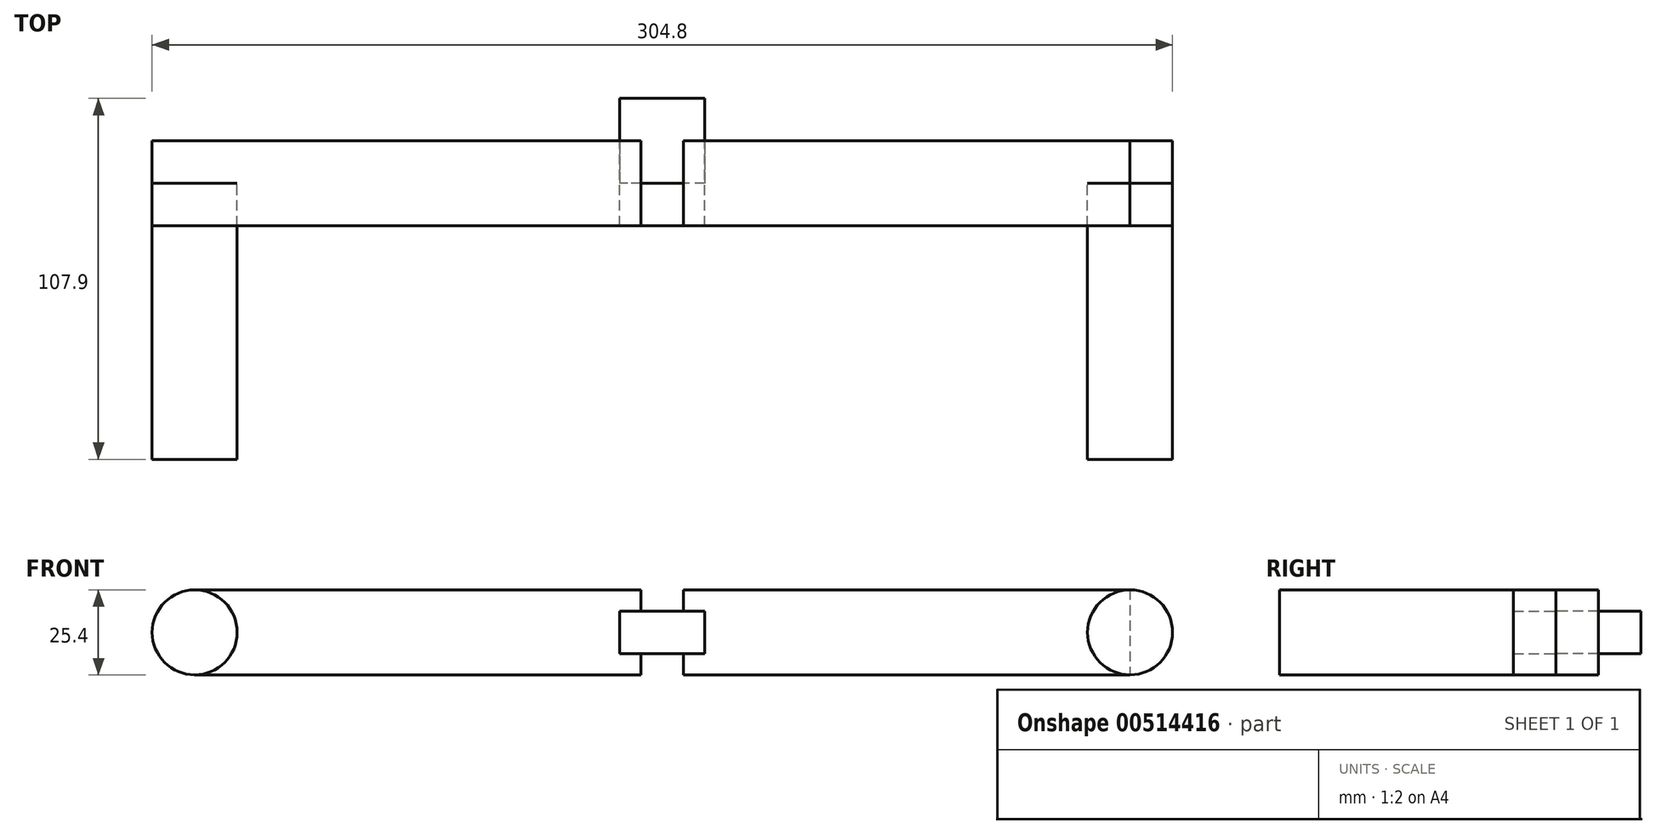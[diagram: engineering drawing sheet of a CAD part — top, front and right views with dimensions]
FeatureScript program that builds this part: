
annotation { "Feature Type Name" : "Feature", "Feature Type Description" : "" }
export const myFeature = defineFeature(function(context is Context, id is Id, definition is map)
    precondition{}
    {
        {
            var Q0;
            Q0=qCreatedBy(makeId("Front.planeOp"),FACE);
            var sketch = newSketch(context, id + "F0", { "sketchPlane" : qUnion([Q0])});
            skLineSegment(sketch, "E0.bottom", {"start": v(-139.7, 12.7) * mm, "end": v(139.7, 12.7) * mm});
            skLineSegment(sketch, "E0.top", {"start": v(-139.7, -12.7) * mm, "end": v(139.7, -12.7) * mm});
            skLineSegment(sketch, "E0.left", {"start": v(-139.7, 12.7) * mm, "end": v(-139.7, -12.7) * mm});
            skLineSegment(sketch, "E0.right", {"start": v(139.7, 12.7) * mm, "end": v(139.7, -12.7) * mm});
            skCircle(sketch, "E1", {"center": v(139.7, 0) * mm, "radius": 12.7 * mm});
            skArc(sketch, "E2", {"start": v(-139.7, 12.7) * mm, "mid": v(-152.4, 0) * mm, "end": v(-139.7, -12.7) * mm});
            skLineSegment(sketch, "E3", {"start": v(-139.7, 0) * mm, "end": v(-152.4, 0) * mm});
            skCircle(sketch, "E4", {"center": v(-139.7, 0) * mm, "radius": 12.7 * mm});
            skLineSegment(sketch, "E5.bottom", {"start": v(139.7, 12.7) * mm, "end": v(139.7, 12.7) * mm});
            skLineSegment(sketch, "E5.top", {"start": v(139.7, -12.7) * mm, "end": v(139.7, -12.7) * mm});
            skLineSegment(sketch, "E6.bottom", {"start": v(6.35, 12.7) * mm, "end": v(-6.35, 12.7) * mm});
            skLineSegment(sketch, "E6.top", {"start": v(6.35, -12.7) * mm, "end": v(-6.35, -12.7) * mm});
            skLineSegment(sketch, "E6.left", {"start": v(6.35, 12.7) * mm, "end": v(6.35, -12.7) * mm});
            skLineSegment(sketch, "E6.right", {"start": v(-6.35, 12.7) * mm, "end": v(-6.35, -12.7) * mm});
            skLineSegment(sketch, "E7.bottom", {"start": v(12.7, 6.35) * mm, "end": v(-12.7, 6.35) * mm});
            skLineSegment(sketch, "E7.top", {"start": v(12.7, -6.35) * mm, "end": v(-12.7, -6.35) * mm});
            skLineSegment(sketch, "E7.left", {"start": v(12.7, 6.35) * mm, "end": v(12.7, -6.35) * mm});
            skLineSegment(sketch, "E7.right", {"start": v(-12.7, 6.35) * mm, "end": v(-12.7, -6.35) * mm});
            skSolve(sketch);
        }
        {
            var Q0;
            {var subQ3=sQuery(id+"F0.wireOp",EDGE,"E3");Q0=makeQuery(id+"F0.imprint","IMPRINT",FACE,{"disambiguationData":[TD([[makeQuery(id+"F0.imprint","IMPRINT",EDGE,{"derivedFrom":subQ3}),-1.0]])]});}
            var Q1;
            {var subQ1=sQuery(id+"F0.wireOp",EDGE,"E0.left");var subQ3=makeQuery(id+"F0.imprint","INTERSECT",VERTEX,{"derivedFrom":[subQ1,sQuery(id+"F0.wireOp",EDGE,"E3")]});Q1=makeQuery(id+"F0.imprint","IMPRINT",FACE,{"disambiguationData":[TD([[makeQuery(id+"F0.imprint","IMPRINT",EDGE,{"disambiguationData":[TD([[subQ3,1.0]])],"derivedFrom":subQ1}),1.0]])]});}
            var Q2;
            {var subQ3=sQuery(id+"F0.wireOp",EDGE,"E3");Q2=makeQuery(id+"F0.imprint","IMPRINT",FACE,{"disambiguationData":[TD([[makeQuery(id+"F0.imprint","IMPRINT",EDGE,{"derivedFrom":subQ3}),1.0]])]});}
            var Q3;
            {var subQ0=sQuery(id+"F0.wireOp",EDGE,"E1");var subQ1=makeQuery(id+"F0.imprint","INTERSECT",VERTEX,{"derivedFrom":[sQuery(id+"F0.wireOp",EDGE,"E0.bottom"),subQ0]});Q3=makeQuery(id+"F0.imprint","IMPRINT",FACE,{"disambiguationData":[TD([[makeQuery(id+"F0.imprint","IMPRINT",EDGE,{"disambiguationData":[TD([[subQ1,-1.0]])],"derivedFrom":subQ0}),1.0]])]});}
            var Q4;
            {var subQ0=sQuery(id+"F0.wireOp",EDGE,"E0.right");Q4=makeQuery(id+"F0.imprint","IMPRINT",FACE,{"disambiguationData":[TD([[makeQuery(id+"F0.imprint","IMPRINT",EDGE,{"derivedFrom":subQ0}),1.0]])]});}
            var Q5;
            {var subQ0=sQuery(id+"F0.wireOp",EDGE,"E0.right");Q5=makeQuery(id+"F0.imprint","IMPRINT",FACE,{"disambiguationData":[TD([[makeQuery(id+"F0.imprint","IMPRINT",EDGE,{"derivedFrom":subQ0}),1.0]])]});}
            var Q6;
            {var subQ0=sQuery(id+"F0.wireOp",EDGE,"E0.left");var subQ4=makeQuery(id+"F0.imprint","INTERSECT",VERTEX,{"derivedFrom":[sQuery(id+"F0.wireOp",EDGE,"E3"),subQ0]});Q6=makeQuery(id+"F0.imprint","IMPRINT",FACE,{"disambiguationData":[TD([[makeQuery(id+"F0.imprint","IMPRINT",EDGE,{"disambiguationData":[TD([[subQ4,1.0]])],"derivedFrom":subQ0}),1.0]])]});}
            var Q7;
            Q7=sQuery(id+"F0.wireOp",EDGE,"E1");
            extrude(context, id + "F1", {"entities" : qUnion([Q0, Q1, Q2, Q3, Q4, Q5, Q6]), "surfaceEntities" : qUnion([Q7]), "depth" : 82.5 * mm, "offsetDistance" : 25.4 * mm});
        }
        {
            var Q0;
            {var subQ2=sQuery(id+"F0.wireOp",EDGE,"E0.bottom");var subQ4=sQuery(id+"F0.wireOp",EDGE,"E1");var subQ5=makeQuery(id+"F0.imprint","INTERSECT",VERTEX,{"derivedFrom":[subQ2,subQ4]});Q0=makeQuery(id+"F0.imprint","IMPRINT",FACE,{"disambiguationData":[TD([[makeQuery(id+"F0.imprint","IMPRINT",EDGE,{"disambiguationData":[TD([[subQ5,-1.0]])],"derivedFrom":subQ4}),-1.0]])]});}
            var Q1;
            {var subQ0=sQuery(id+"F0.wireOp",EDGE,"E0.right");Q1=makeQuery(id+"F0.imprint","IMPRINT",FACE,{"disambiguationData":[TD([[makeQuery(id+"F0.imprint","IMPRINT",EDGE,{"derivedFrom":subQ0}),-1.0]])]});}
            var Q2;
            {var subQ1=sQuery(id+"F0.wireOp",EDGE,"5lEPmECd-of7d-YvdJ-hnNs-EzF3xCs3axzf.bottom");Q2=makeQuery(id+"F0.imprint","IMPRINT",FACE,{"disambiguationData":[TD([[makeQuery(id+"F0.imprint","IMPRINT",EDGE,{"derivedFrom":subQ1}),-1.0]])]});}
            var Q3;
            Q3=makeQuery(id+"F0.imprint","IMPRINT",FACE,{"disambiguationData":[TD([[makeQuery(id+"F0.imprint","IMPRINT",EDGE,{"derivedFrom":sQuery(id+"F0.wireOp",EDGE,"5lEPmECd-of7d-YvdJ-hnNs-EzF3xCs3axzf.right")}),1.0]])]});
            var Q4;
            {var subQ0=sQuery(id+"F0.wireOp",EDGE,"E0.right");Q4=makeQuery(id+"F0.imprint","IMPRINT",FACE,{"disambiguationData":[TD([[makeQuery(id+"F0.imprint","IMPRINT",EDGE,{"derivedFrom":subQ0}),-1.0]])]});}
            var Q5;
            {var subQ0=sQuery(id+"F0.wireOp",EDGE,"E0.right");Q5=makeQuery(id+"F0.imprint","IMPRINT",FACE,{"disambiguationData":[TD([[makeQuery(id+"F0.imprint","IMPRINT",EDGE,{"derivedFrom":subQ0}),1.0]])]});}
            var Q6;
            {var subQ1=sQuery(id+"F0.wireOp",EDGE,"A2jTNkQ9-ff6S-K6zJ-Aq4Z-fCkLy7TxGZE3.bottom");Q6=makeQuery(id+"F0.imprint","IMPRINT",FACE,{"disambiguationData":[TD([[makeQuery(id+"F0.imprint","IMPRINT",EDGE,{"derivedFrom":subQ1}),1.0]])]});}
            var Q7;
            {var subQ0=sQuery(id+"F0.wireOp",EDGE,"E3");Q7=makeQuery(id+"F0.imprint","IMPRINT",FACE,{"disambiguationData":[TD([[makeQuery(id+"F0.imprint","IMPRINT",EDGE,{"derivedFrom":subQ0}),-1.0]])]});}
            var Q8;
            {var subQ0=sQuery(id+"F0.wireOp",EDGE,"E3");Q8=makeQuery(id+"F0.imprint","IMPRINT",FACE,{"disambiguationData":[TD([[makeQuery(id+"F0.imprint","IMPRINT",EDGE,{"derivedFrom":subQ0}),1.0]])]});}
            var Q9;
            {var subQ0=sQuery(id+"F0.wireOp",EDGE,"A2jTNkQ9-ff6S-K6zJ-Aq4Z-fCkLy7TxGZE3.right");Q9=makeQuery(id+"F0.imprint","IMPRINT",FACE,{"disambiguationData":[TD([[makeQuery(id+"F0.imprint","IMPRINT",EDGE,{"derivedFrom":subQ0}),1.0]])]});}
            var Q10;
            {var subQ0=sQuery(id+"F0.wireOp",EDGE,"A2jTNkQ9-ff6S-K6zJ-Aq4Z-fCkLy7TxGZE3.right");Q10=makeQuery(id+"F0.imprint","IMPRINT",FACE,{"disambiguationData":[TD([[makeQuery(id+"F0.imprint","IMPRINT",EDGE,{"derivedFrom":subQ0}),-1.0]])]});}
            var Q11;
            {var subQ0=sQuery(id+"F0.wireOp",EDGE,"E0.left");var subQ4=makeQuery(id+"F0.imprint","INTERSECT",VERTEX,{"derivedFrom":[sQuery(id+"F0.wireOp",EDGE,"E3"),subQ0]});Q11=makeQuery(id+"F0.imprint","IMPRINT",FACE,{"disambiguationData":[TD([[makeQuery(id+"F0.imprint","IMPRINT",EDGE,{"disambiguationData":[TD([[subQ4,1.0]])],"derivedFrom":subQ0}),1.0]])]});}
            var Q12;
            {var subQ13=sQuery(id+"F0.wireOp",EDGE,"E7.right");Q12=makeQuery(id+"F0.imprint","IMPRINT",FACE,{"disambiguationData":[TD([[makeQuery(id+"F0.imprint","IMPRINT",EDGE,{"derivedFrom":subQ13}),-1.0]])]});}
            var Q13;
            {var subQ10=sQuery(id+"F0.wireOp",EDGE,"E6.bottom");Q13=makeQuery(id+"F0.imprint","IMPRINT",FACE,{"disambiguationData":[TD([[makeQuery(id+"F0.imprint","IMPRINT",EDGE,{"derivedFrom":subQ10}),-1.0]])]});}
            extrude(context, id + "F2", {"entities" : qUnion([Q0, Q1, Q2, Q3, Q4, Q5, Q6, Q7, Q8, Q9, Q10, Q11, Q12, Q13]), "depth" : 25.4 * mm, "offsetDistance" : 25.4 * mm, "symmetric" : true});
        }
        {
            var Q0;
            {var subQ1=sQuery(id+"F0.wireOp",EDGE,"E0.left");var subQ3=makeQuery(id+"F0.imprint","INTERSECT",VERTEX,{"derivedFrom":[subQ1,sQuery(id+"F0.wireOp",EDGE,"E3")]});Q0=makeQuery(id+"F0.imprint","IMPRINT",FACE,{"disambiguationData":[TD([[makeQuery(id+"F0.imprint","IMPRINT",EDGE,{"disambiguationData":[TD([[subQ3,1.0]])],"derivedFrom":subQ1}),1.0]])]});}
            var Q1;
            {var subQ3=sQuery(id+"F0.wireOp",EDGE,"E3");Q1=makeQuery(id+"F0.imprint","IMPRINT",FACE,{"disambiguationData":[TD([[makeQuery(id+"F0.imprint","IMPRINT",EDGE,{"derivedFrom":subQ3}),-1.0]])]});}
            var Q2;
            {var subQ3=sQuery(id+"F0.wireOp",EDGE,"E3");Q2=makeQuery(id+"F0.imprint","IMPRINT",FACE,{"disambiguationData":[TD([[makeQuery(id+"F0.imprint","IMPRINT",EDGE,{"derivedFrom":subQ3}),1.0]])]});}
            var Q3;
            {var subQ0=sQuery(id+"F0.wireOp",EDGE,"E0.right");Q3=makeQuery(id+"F0.imprint","IMPRINT",FACE,{"disambiguationData":[TD([[makeQuery(id+"F0.imprint","IMPRINT",EDGE,{"derivedFrom":subQ0}),1.0]])]});}
            extrude(context, id + "F3", {"entities" : qUnion([Q0, Q1, Q2, Q3]), "depth" : 25.4 * mm, "offsetDistance" : 25.4 * mm, "symmetric" : true});
        }
        {
            var Q0;
            {var subQ5=sQuery(id+"F0.wireOp",EDGE,"E7.right");Q0=makeQuery(id+"F0.imprint","IMPRINT",FACE,{"disambiguationData":[TD([[makeQuery(id+"F0.imprint","IMPRINT",EDGE,{"derivedFrom":subQ5}),1.0]])]});}
            var Q1;
            {var subQ0=sQuery(id+"F0.wireOp",EDGE,"E7.bottom");var subQ1=sQuery(id+"F0.wireOp",EDGE,"E6.left");var subQ2=makeQuery(id+"F0.imprint","INTERSECT",VERTEX,{"derivedFrom":[subQ1,subQ0]});Q1=makeQuery(id+"F0.imprint","IMPRINT",FACE,{"disambiguationData":[TD([[makeQuery(id+"F0.imprint","IMPRINT",EDGE,{"disambiguationData":[TD([[subQ2,-1.0]])],"derivedFrom":subQ1}),-1.0]])]});}
            var Q2;
            {var subQ0=sQuery(id+"F0.wireOp",EDGE,"E6.bottom");Q2=makeQuery(id+"F0.imprint","IMPRINT",FACE,{"disambiguationData":[TD([[makeQuery(id+"F0.imprint","IMPRINT",EDGE,{"derivedFrom":subQ0}),1.0]])]});}
            var Q3;
            {var subQ5=sQuery(id+"F0.wireOp",EDGE,"E7.left");Q3=makeQuery(id+"F0.imprint","IMPRINT",FACE,{"disambiguationData":[TD([[makeQuery(id+"F0.imprint","IMPRINT",EDGE,{"derivedFrom":subQ5}),-1.0]])]});}
            var Q4;
            {var subQ0=sQuery(id+"F0.wireOp",EDGE,"E6.top");Q4=makeQuery(id+"F0.imprint","IMPRINT",FACE,{"disambiguationData":[TD([[makeQuery(id+"F0.imprint","IMPRINT",EDGE,{"derivedFrom":subQ0}),-1.0]])]});}
            extrude(context, id + "F4", {"entities" : qUnion([Q0, Q1, Q2, Q3, Q4]), "oppositeDirection" : true, "depth" : 25.4 * mm, "offsetDistance" : 25.4 * mm});
        }
        {
            var Q0;
            {var subQ5=sQuery(id+"F0.wireOp",EDGE,"E7.left");Q0=makeQuery(id+"F0.imprint","IMPRINT",FACE,{"disambiguationData":[TD([[makeQuery(id+"F0.imprint","IMPRINT",EDGE,{"derivedFrom":subQ5}),-1.0]])]});}
            var Q1;
            {var subQ0=sQuery(id+"F0.wireOp",EDGE,"E6.top");Q1=makeQuery(id+"F0.imprint","IMPRINT",FACE,{"disambiguationData":[TD([[makeQuery(id+"F0.imprint","IMPRINT",EDGE,{"derivedFrom":subQ0}),-1.0]])]});}
            var Q2;
            {var subQ0=sQuery(id+"F0.wireOp",EDGE,"E6.bottom");Q2=makeQuery(id+"F0.imprint","IMPRINT",FACE,{"disambiguationData":[TD([[makeQuery(id+"F0.imprint","IMPRINT",EDGE,{"derivedFrom":subQ0}),1.0]])]});}
            var Q3;
            {var subQ5=sQuery(id+"F0.wireOp",EDGE,"E7.right");Q3=makeQuery(id+"F0.imprint","IMPRINT",FACE,{"disambiguationData":[TD([[makeQuery(id+"F0.imprint","IMPRINT",EDGE,{"derivedFrom":subQ5}),1.0]])]});}
            var Q4;
            {var subQ0=sQuery(id+"F0.wireOp",EDGE,"E7.bottom");var subQ1=sQuery(id+"F0.wireOp",EDGE,"E6.left");var subQ2=makeQuery(id+"F0.imprint","INTERSECT",VERTEX,{"derivedFrom":[subQ1,subQ0]});Q4=makeQuery(id+"F0.imprint","IMPRINT",FACE,{"disambiguationData":[TD([[makeQuery(id+"F0.imprint","IMPRINT",EDGE,{"disambiguationData":[TD([[subQ2,-1.0]])],"derivedFrom":subQ1}),-1.0]])]});}
            extrude(context, id + "F5", {"entities" : qUnion([Q0, Q1, Q2, Q3, Q4]), "depth" : 12.7 * mm, "offsetDistance" : 25.4 * mm});
        }
    });
